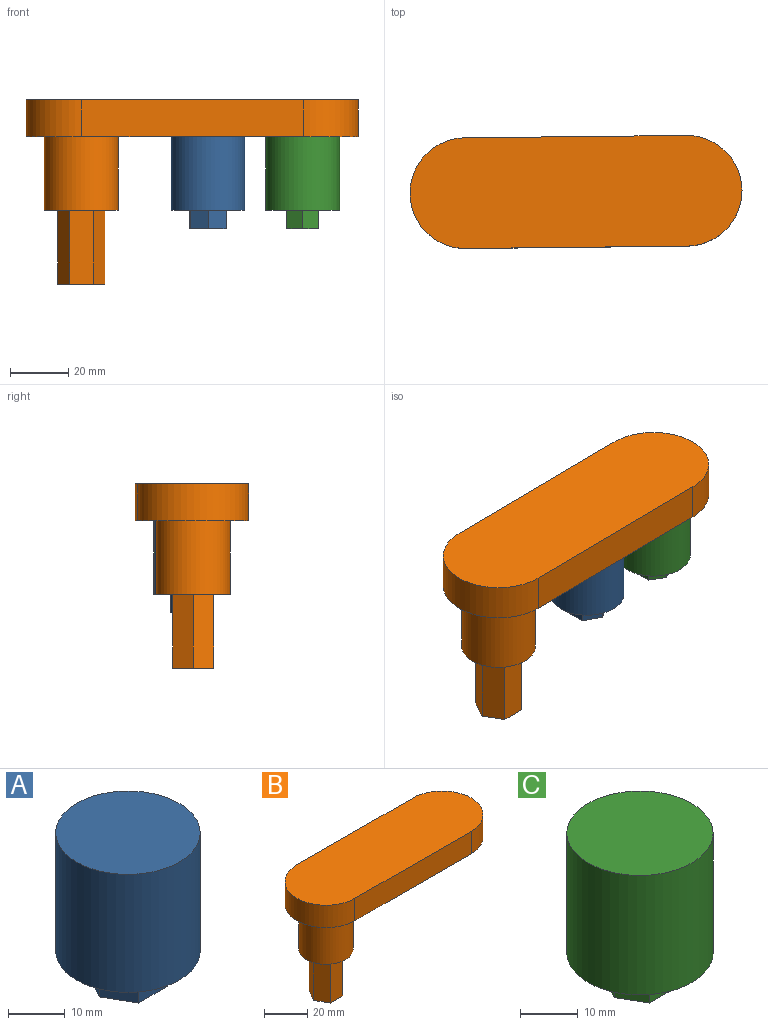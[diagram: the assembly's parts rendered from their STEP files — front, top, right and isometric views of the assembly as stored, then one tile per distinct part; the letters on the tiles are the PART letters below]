
ASSEMBLY  parts=3 mates=2
PART A: 10 faces, bbox 25.4x25.4x31.8 mm
  f0: cylinder r=12.7mm len=25.4mm, axis (0,0,1), area 2026.8mm2, adj f1,f2
  f1: plane 25.4x25.4mm, normal (0,0,-1), area 372.8mm2, adj f0,f3,f4,f5,f6,f7,f8
  f2: plane 25.4x25.4mm, normal (0,0,1), area 506.7mm2, adj f0
  f3: plane 7.18x6.35mm, normal (0,1,0), area 45.6mm2, adj f1,f4,f8,f9
  f4: plane 6.35x6.22mm, normal (0.87,0.5,0), area 45.6mm2, adj f1,f3,f5,f9
  f5: plane 6.35x6.22mm, normal (0.87,-0.5,0), area 45.6mm2, adj f1,f4,f6,f9
  f6: plane 7.18x6.35mm, normal (0,-1,0), area 45.6mm2, adj f1,f5,f7,f9
  f7: plane 6.35x6.22mm, normal (-0.87,-0.5,0), area 45.6mm2, adj f1,f6,f8,f9
  f8: plane 6.35x6.22mm, normal (-0.87,0.5,0), area 45.6mm2, adj f1,f3,f7,f9
  f9: plane 14.36x12.44mm, normal (0,0,-1), area 133.9mm2, adj f3,f4,f5,f6,f7,f8
PART B: 15 faces, bbox 114.3x38.1x63.5 mm
  f0: plane 25.4x25.4mm, normal (0,0,-1), area 335.6mm2, adj f1,f2,f3,f4,f5,f6,f7
  f1: cylinder r=12.7mm len=25.4mm, axis (0,0,-1), area 2026.8mm2, adj f0,f14
  f2: plane 25.4x8.12mm, normal (0,1,0), area 206.1mm2, adj f0,f3,f7,f8
  f3: plane 25.4x7.03mm, normal (0.87,0.5,0), area 206.1mm2, adj f0,f2,f4,f8
  f4: plane 25.4x7.03mm, normal (0.87,-0.5,0), area 206.1mm2, adj f0,f3,f5,f8
  f5: plane 25.4x8.12mm, normal (0,-1,0), area 206.1mm2, adj f0,f4,f6,f8
  f6: plane 25.4x7.03mm, normal (-0.87,-0.5,0), area 206.1mm2, adj f0,f5,f7,f8
  f7: plane 25.4x7.03mm, normal (-0.87,0.5,0), area 206.1mm2, adj f0,f2,f6,f8
  f8: plane 16.23x14.06mm, normal (0,0,-1), area 171.1mm2, adj f2,f3,f4,f5,f6,f7
  f9: plane 76.2x12.7mm, normal (0,1,0), area 967.7mm2, adj f10,f12,f13,f14
  f10: cylinder r=19.05mm len=38.1mm, axis (0,0,-1), area 760.1mm2, adj f9,f11,f13,f14
  f11: plane 76.2x12.7mm, normal (0,-1,0), area 967.7mm2, adj f10,f12,f13,f14
  f12: cylinder r=19.05mm len=38.1mm, axis (0,0,-1), area 760.1mm2, adj f9,f11,f13,f14
  f13: plane 114.3x38.1mm, normal (0,0,1), area 4043.3mm2, adj f9,f10,f11,f12
  f14: plane 114.3x38.1mm, normal (0,0,-1), area 3536.6mm2, adj f1,f9,f10,f11,f12
PART C: 10 faces, bbox 25.4x25.4x31.8 mm
  f0: cylinder r=12.7mm len=25.4mm, axis (0,0,1), area 2026.8mm2, adj f1,f2
  f1: plane 25.4x25.4mm, normal (0,0,-1), area 402mm2, adj f0,f3,f4,f5,f6,f7,f8
  f2: plane 25.4x25.4mm, normal (0,0,1), area 506.7mm2, adj f0
  f3: plane 6.35x6.35mm, normal (0,1,0), area 40.3mm2, adj f1,f4,f8,f9
  f4: plane 6.35x5.5mm, normal (0.87,0.5,0), area 40.3mm2, adj f1,f3,f5,f9
  f5: plane 6.35x5.5mm, normal (0.87,-0.5,0), area 40.3mm2, adj f1,f4,f6,f9
  f6: plane 6.35x6.35mm, normal (0,-1,0), area 40.3mm2, adj f1,f5,f7,f9
  f7: plane 6.35x5.5mm, normal (-0.87,-0.5,0), area 40.3mm2, adj f1,f6,f8,f9
  f8: plane 6.35x5.5mm, normal (-0.87,0.5,0), area 40.3mm2, adj f1,f3,f7,f9
  f9: plane 12.7x11mm, normal (0,0,-1), area 104.7mm2, adj f3,f4,f5,f6,f7,f8
PLACE A rot(axis=(0,0,-1),88.8deg) t=(42.74,38.56,0)mm
PLACE B rot(axis=(0,0,1),0.6deg) t=(0,0,0)mm
PLACE C rot(axis=(0,0,1),90deg) t=(76.2,-75.38,0)mm
MATE revolute A.f0 <-> B.f14  axis (0,0,1) through (43.56,0.47,25.4)mm
MATE revolute C.f0 <-> B.f12  axis (0,0,1) through (76.2,0.82,25.4)mm
